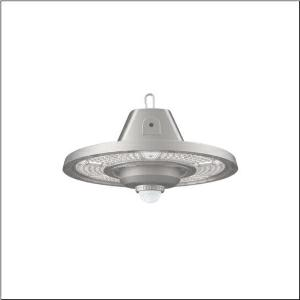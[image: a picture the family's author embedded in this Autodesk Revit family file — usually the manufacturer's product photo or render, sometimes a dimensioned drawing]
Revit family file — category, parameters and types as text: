
# Revit family: highbay_31-s_51hc427a4fmb01
name_source: partatom
category: Lighting Fixtures
units: mm (PartAtom-declared; Revit-internal decimal feet)

## family parameters
Cut with Voids When Loaded = No
Host = Face
Light Source = No
Part Type = Normal
Room Calculation Point = No
Round Connector Dimension = Use Diameter
Shared = No

## types (1)
- Highbay 31-S (1 x LED, 14000 lm, 94 W, 4000K)
    Apparent Load = 94 VA
    CIE Flux Codes = 77 99 100 100 100
    Color Rendering = 80
    Color Temperature = 4000K
    Default Elevation = 1800 mm
    Description = Highbay 31-S, LED high bay luminaire, primary light control with lens, of PC, primary optical cover: cover panel, of PC, transparent, light emission: direct distribution, primary light characteristic: rotationally symmetric, installation type: suspended mounting, surface-mounted, LED, rated luminous flux: 14.000lm, luminous efficacy: 150lm/W, light colour: 840, colour temperature: 4000K, control gear: ECG, with cable, 3x 1.0mm², free wire ends, mains connection: 220..240V, AC/DC, 0/50..60Hz, cable length: 1,5m, rated input power: 94W, housing, rotationally symmetric, of diecast aluminium, powder-coated, grey aluminium (RAL 9007), with hook on luminaire side, incl. screw, diameter: 339mm, PIR sensor, protection rating (complete): IP65, insulation class (complete): insulation class I (protective earthing), certification: CE, ENEC, UKCA, protection symbol: D, impact resistance: IK08, permissible operating ambient temperature: -30..+45°C, standard: EN 60598-2-22, EN 60598, corresponds to IFS (International Featured Standards) requirements for safety and quality in the food industry, packaging unit: 1 piece
    Height = 141 mm
    Lamp = 1 x LED
    Lamp Light Flux = 14000 lm
    Lamp Power = 94 W
    Lamp count = 1
    Length = 339 mm
    Luminous efficacy = 149 lm/W
    Manufacturer = Siteco
    ModVariant = No
    Model = 51HC427A4FMB01
    Mounting Place = Ceiling
    Mounting Type = Pendant
    Number of Poles = 1
    OnlyDefault = Yes
    Power Factor = 1
    Product Name = Highbay 31-S
    Product group = LED high bay luminaire
    ProductGroupID = 903
    Protection Class = Protection class I
    Protection Degree = IP 65
    RLX_Detail_Level = 1
    RLX_Emergency_Light_Flux = 0 lm
    RLX_Emergency_Type = 0
    RLX_Emergency_Type_DB = No
    RlxData = <blob elided: 108225 chars, md5=1ba25a56>
    Socket = socket
    Standby Power = 0 W
    System Light Flux = 14000 lm
    System Power = 94 W
    Type Comments = Product without accessories
    Type Image = l_384983.jpg
    URL = http://relux.com
    VarID = ---
    Voltage = 0 V
    Weight = 0.00 kg
    Width = 0 mm  [stored 0 ft]

note: [stored X ft] marks values corroborated as IEEE doubles in the binary element streams (Revit-internal decimal feet)

## geometry (parser evidence)
native form markers: Blend x4, Sweep x9
no freeform markers — native parametric forms only
